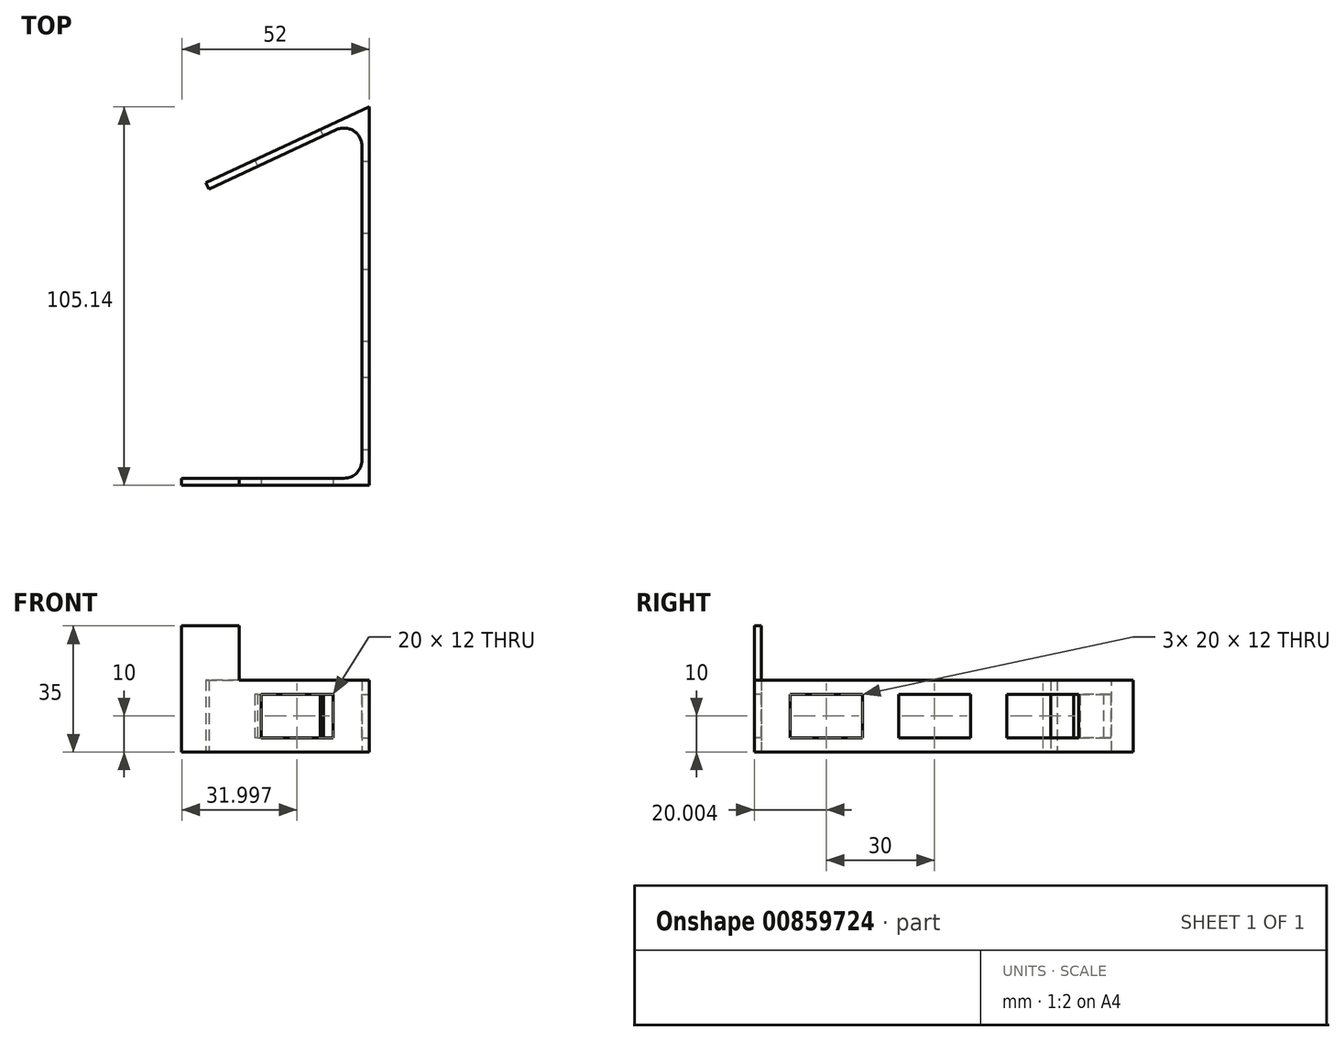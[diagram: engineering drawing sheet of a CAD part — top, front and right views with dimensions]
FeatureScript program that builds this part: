
annotation { "Feature Type Name" : "Feature", "Feature Type Description" : "" }
export const myFeature = defineFeature(function(context is Context, id is Id, definition is map)
    precondition{}
    {
        {
            var Q0;
            Q0=qCreatedBy(makeId("Top.planeOp"),FACE);
            var sketch = newSketch(context, id + "F0", { "sketchPlane" : qUnion([Q0])});
            skLineSegment(sketch, "E0", {"start": v(-29.57, -51.68) * mm, "end": v(20.43, -51.68) * mm});
            skLineSegment(sketch, "E1", {"start": v(20.43, -51.68) * mm, "end": v(20.43, 48.32) * mm});
            skLineSegment(sketch, "E2", {"start": v(20.43, 48.32) * mm, "end": v(-22.04, 28.52) * mm});
            skLineSegment(sketch, "E3", {"start": v(-22.04, 28.52) * mm, "end": v(-22.89, 30.33) * mm});
            skLineSegment(sketch, "E4", {"start": v(-22.89, 30.33) * mm, "end": v(22.43, 51.46) * mm});
            skLineSegment(sketch, "E5", {"start": v(22.43, 51.46) * mm, "end": v(22.43, -53.68) * mm});
            skLineSegment(sketch, "E6", {"start": v(22.43, -53.68) * mm, "end": v(-29.57, -53.68) * mm});
            skLineSegment(sketch, "E7", {"start": v(-29.57, -53.68) * mm, "end": v(-29.57, -51.68) * mm});
            skSolve(sketch);
        }
        {
            var Q0;
            Q0=makeQuery(id+"F0.imprint","IMPRINT",FACE,{"disambiguationData":[TD([[makeQuery(id+"F0.imprint","IMPRINT",EDGE,{"derivedFrom":sQuery(id+"F0.wireOp",EDGE,"E0")}),-1.0]])]});
            extrude(context, id + "F1", {"entities" : qUnion([Q0]), "depth" : 20 * mm, "offsetDistance" : 25 * mm});
        }
        {
            var Q0;
            Q0=makeQuery(id+"F1.opExtrude","SWEPT_EDGE",EDGE,{"disambiguationData":[OSD([sQuery(id+"F0.wireOp",EDGE,"E1"),sQuery(id+"F0.wireOp",EDGE,"E2")])]});
            var Q1;
            Q1=makeQuery(id+"F1.opExtrude","SWEPT_EDGE",EDGE,{"disambiguationData":[OSD([sQuery(id+"F0.wireOp",EDGE,"E0"),sQuery(id+"F0.wireOp",EDGE,"E1")])]});
            fillet(context, id + "F2", {"entities" : qUnion([Q0, Q1]), "radius" : 5 * mm, "tangentPropagation" : true, "allowEdgeOverflow" : false});
        }
        {
            var Q0;
            Q0=makeQuery(id+"F1.opExtrude","CAP_FACE",FACE,{"disambiguationData":[OSD([sQuery(id+"F0.wireOp",EDGE,"E0"),sQuery(id+"F0.wireOp",EDGE,"E1"),sQuery(id+"F0.wireOp",EDGE,"E2"),sQuery(id+"F0.wireOp",EDGE,"E3"),sQuery(id+"F0.wireOp",EDGE,"E4"),sQuery(id+"F0.wireOp",EDGE,"E5"),sQuery(id+"F0.wireOp",EDGE,"E6"),sQuery(id+"F0.wireOp",EDGE,"E7")])],"isStart":false});
            var sketch = newSketch(context, id + "F3", { "sketchPlane" : qUnion([Q0])});
            skLineSegment(sketch, "E8", {"start": v(-13.63, -51.68) * mm, "end": v(-13.63, -53.68) * mm});
            skLineSegment(sketch, "E9", {"start": v(-13.63, -53.68) * mm, "end": v(-29.57, -53.68) * mm});
            skLineSegment(sketch, "E10", {"start": v(-29.57, -53.68) * mm, "end": v(-29.57, -51.68) * mm});
            skLineSegment(sketch, "E11", {"start": v(-29.57, -51.68) * mm, "end": v(-13.63, -51.68) * mm});
            skSolve(sketch);
        }
        {
            var Q0;
            Q0=makeQuery(id+"F3.imprint","IMPRINT",FACE,{"disambiguationData":[TD([[makeQuery(id+"F3.imprint","IMPRINT",EDGE,{"derivedFrom":sQuery(id+"F3.wireOp",EDGE,"E8")}),-1.0]])]});
            extrude(context, id + "F4", {"entities" : qUnion([Q0]), "operationType" : NewBodyOperationType.ADD, "depth" : 15 * mm, "offsetDistance" : 25 * mm});
        }
        {
            var Q0;
            Q0=makeQuery(id+"F1.opExtrude","SWEPT_FACE",FACE,{"disambiguationData":[OSD([sQuery(id+"F0.wireOp",EDGE,"E5")])]});
            var sketch = newSketch(context, id + "F5", { "sketchPlane" : qUnion([Q0])});
            skLineSegment(sketch, "E12.bottom", {"start": v(-43.68, 16) * mm, "end": v(-23.68, 16) * mm});
            skLineSegment(sketch, "E12.top", {"start": v(-43.68, 4) * mm, "end": v(-23.68, 4) * mm});
            skLineSegment(sketch, "E12.left", {"start": v(-43.68, 16) * mm, "end": v(-43.68, 4) * mm});
            skLineSegment(sketch, "E12.right", {"start": v(-23.68, 16) * mm, "end": v(-23.68, 4) * mm});
            skLineSegment(sketch, "E13.bottom", {"start": v(-13.68, 16) * mm, "end": v(6.32, 16) * mm});
            skLineSegment(sketch, "E13.top", {"start": v(-13.68, 4) * mm, "end": v(6.32, 4) * mm});
            skLineSegment(sketch, "E13.left", {"start": v(-13.68, 16) * mm, "end": v(-13.68, 4) * mm});
            skLineSegment(sketch, "E13.right", {"start": v(6.32, 16) * mm, "end": v(6.32, 4) * mm});
            skLineSegment(sketch, "E14.bottom", {"start": v(16.32, 4) * mm, "end": v(36.32, 4) * mm});
            skLineSegment(sketch, "E14.top", {"start": v(16.32, 16) * mm, "end": v(36.32, 16) * mm});
            skLineSegment(sketch, "E14.left", {"start": v(16.32, 4) * mm, "end": v(16.32, 16) * mm});
            skLineSegment(sketch, "E14.right", {"start": v(36.32, 4) * mm, "end": v(36.32, 16) * mm});
            skSolve(sketch);
        }
        {
            var Q0;
            Q0=makeQuery(id+"F5.imprint","IMPRINT",FACE,{"disambiguationData":[TD([[makeQuery(id+"F5.imprint","IMPRINT",EDGE,{"derivedFrom":sQuery(id+"F5.wireOp",EDGE,"E12.bottom")}),-1.0]])]});
            var Q1;
            Q1=makeQuery(id+"F5.imprint","IMPRINT",FACE,{"disambiguationData":[TD([[makeQuery(id+"F5.imprint","IMPRINT",EDGE,{"derivedFrom":sQuery(id+"F5.wireOp",EDGE,"E13.bottom")}),-1.0]])]});
            var Q2;
            Q2=makeQuery(id+"F5.imprint","IMPRINT",FACE,{"disambiguationData":[TD([[makeQuery(id+"F5.imprint","IMPRINT",EDGE,{"derivedFrom":sQuery(id+"F5.wireOp",EDGE,"E14.bottom")}),1.0]])]});
            extrude(context, id + "F6", {"entities" : qUnion([Q0, Q1, Q2]), "operationType" : NewBodyOperationType.REMOVE, "endBound" : BoundingType.UP_TO_NEXT, "oppositeDirection" : true, "depth" : 17.6 * mm, "offsetDistance" : 25 * mm});
        }
        {
            var Q0;
            Q0=makeQuery(id+"F1.opExtrude","SWEPT_FACE",FACE,{"disambiguationData":[OSD([sQuery(id+"F0.wireOp",EDGE,"E4")])]});
            var sketch = newSketch(context, id + "F7", { "sketchPlane" : qUnion([Q0])});
            skLineSegment(sketch, "E15.bottom", {"start": v(-27.12, 16) * mm, "end": v(-7.12, 16) * mm});
            skLineSegment(sketch, "E15.top", {"start": v(-27.12, 4) * mm, "end": v(-7.12, 4) * mm});
            skLineSegment(sketch, "E15.left", {"start": v(-27.12, 16) * mm, "end": v(-27.12, 4) * mm});
            skLineSegment(sketch, "E15.right", {"start": v(-7.12, 16) * mm, "end": v(-7.12, 4) * mm});
            skSolve(sketch);
        }
        {
            var Q0;
            Q0 = qSketchRegion(id + "F7", true);
            extrude(context, id + "F8", {"entities" : qUnion([Q0]), "operationType" : NewBodyOperationType.REMOVE, "oppositeDirection" : true, "depth" : 15.2 * mm, "offsetDistance" : 25 * mm});
        }
        {
            var Q0;
            Q0=makeQuery(id+"F4.boolean.opBoolean","MERGE",FACE,{"derivedFrom":[makeQuery(id+"F1.opExtrude","SWEPT_FACE",FACE,{"disambiguationData":[OSD([sQuery(id+"F0.wireOp",EDGE,"E6")])]}),makeQuery(id+"F4.opExtrude","SWEPT_FACE",FACE,{"disambiguationData":[OSD([sQuery(id+"F3.wireOp",EDGE,"E9")])]})]});
            var sketch = newSketch(context, id + "F9", { "sketchPlane" : qUnion([Q0])});
            skLineSegment(sketch, "E16.bottom", {"start": v(-7.57, 16) * mm, "end": v(12.43, 16) * mm});
            skLineSegment(sketch, "E16.top", {"start": v(-7.57, 4) * mm, "end": v(12.43, 4) * mm});
            skLineSegment(sketch, "E16.left", {"start": v(-7.57, 16) * mm, "end": v(-7.57, 4) * mm});
            skLineSegment(sketch, "E16.right", {"start": v(12.43, 16) * mm, "end": v(12.43, 4) * mm});
            skSolve(sketch);
        }
        {
            var Q0;
            Q0=makeQuery(id+"F9.imprint","IMPRINT",FACE,{"disambiguationData":[TD([[makeQuery(id+"F9.imprint","IMPRINT",EDGE,{"derivedFrom":sQuery(id+"F9.wireOp",EDGE,"E16.bottom")}),-1.0]])]});
            extrude(context, id + "F10", {"entities" : qUnion([Q0]), "operationType" : NewBodyOperationType.REMOVE, "oppositeDirection" : true, "depth" : 25 * mm, "offsetDistance" : 25 * mm});
        }
    });
